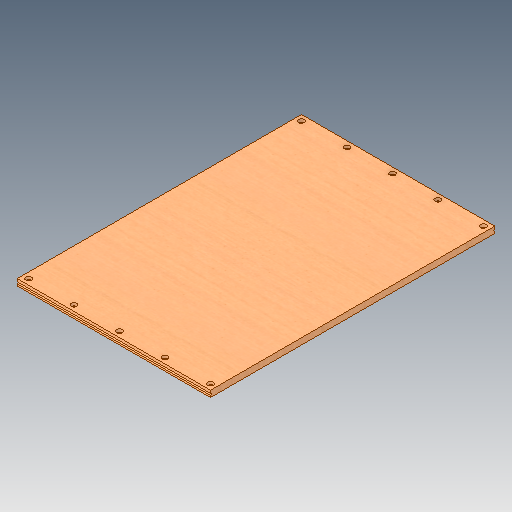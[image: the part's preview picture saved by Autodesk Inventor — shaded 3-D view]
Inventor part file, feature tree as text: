
AUTODESK INVENTOR PART (.ipt)
format: ipt  version: 2018.2 (Build 222227000, 227)  size: 206,848 bytes
history: native  units: mm
features: sketch x3, extrude x2, projected_geometry x2, hole x1, pattern_linear x1, mirror x1
ambient origin geometry x8: Origin, YZ Plane, XZ Plane, XY Plane, X Axis, Y Axis, Z Axis, Center Point
bodies: Solid1 (feature_tree)
feature tree (10):
  extrude  "Extrusion1"  Depth=500.0mm
  hole  "Hole1"  [1 undecoded]
  pattern_linear  "Rectangular Pattern1"  Spacing1=10.0mm  [1 undecoded]
  extrude  "oRingGroove"  Depth=10.0mm
  mirror  "Mirror1"
  sketch  "Sketch1"  dims[d0=340.0mm d1=500.0mm]
  sketch  "Sketch2"  dims[d2=11.1125mm d3=0.0mm]
  projected_geometry  "Projected Loop1"
  sketch  "Sketch3"  dims[d4=10.0mm d5=10.0mm d6=5.5mm d7=6.0mm d8=10.0mm d9=5.0mm d10=90.0deg d11=8.0mm d12=20.594885mm d13=20.0mm d15=480.0mm d16=50.0mm d18=80.0mm d19=1.5875mm d20=6.35mm d21=10.0mm d22=0.0mm]
  projected_geometry  "Projected Loop2"
note: 2 required parameter values undecoded (feature->parameter linkage not recoverable at this tier; creation-order binding heuristic only, values carry confidence <= 0.55)
